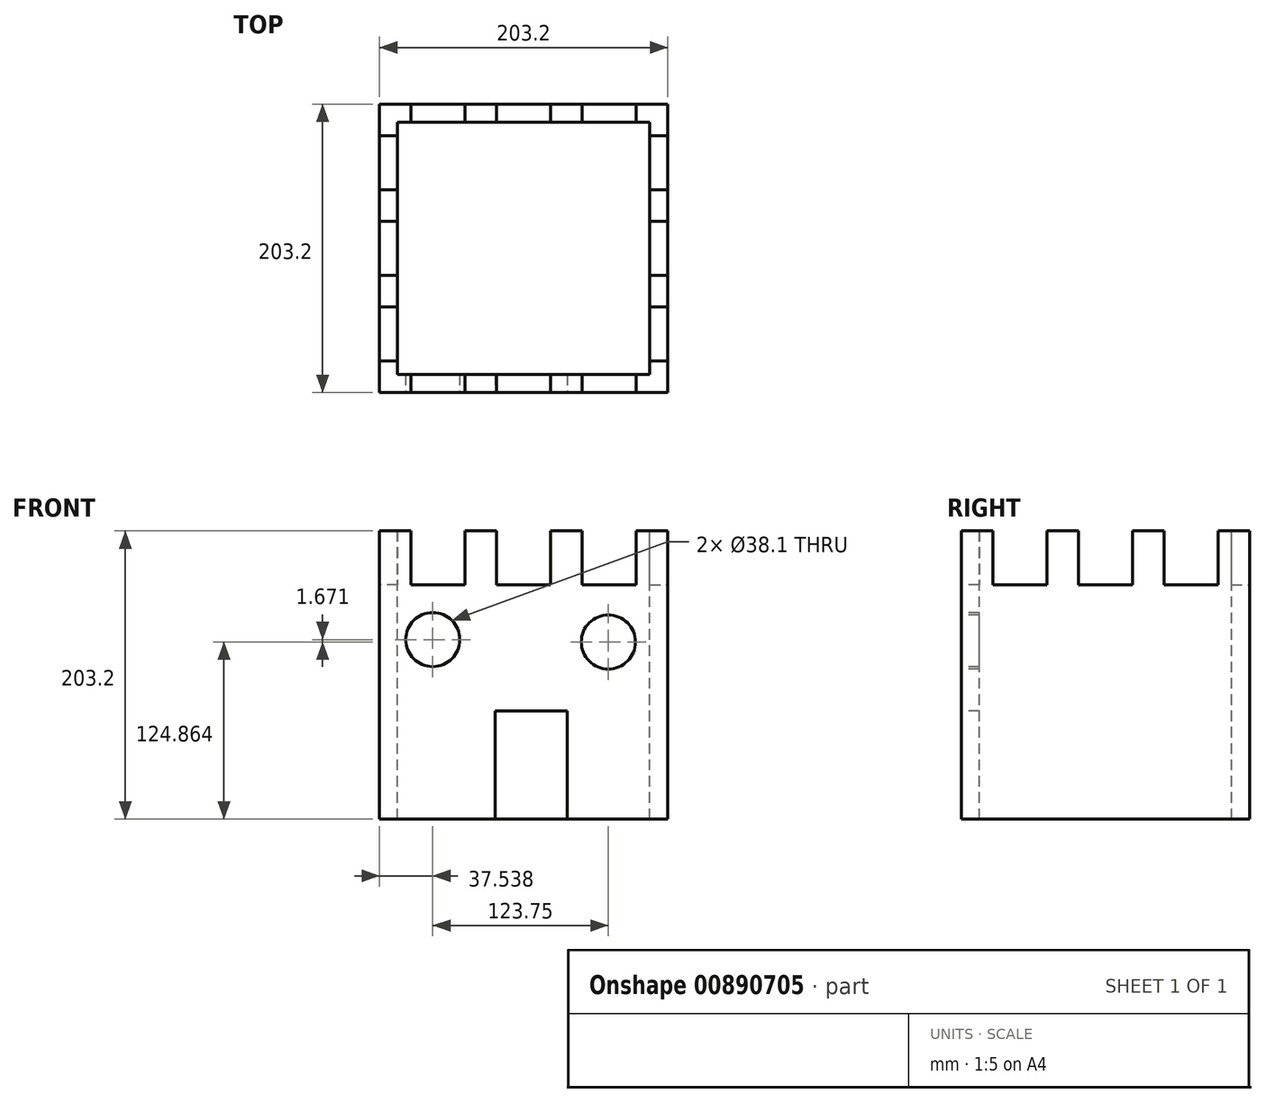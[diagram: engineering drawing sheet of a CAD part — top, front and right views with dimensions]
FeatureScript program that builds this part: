
annotation { "Feature Type Name" : "Feature", "Feature Type Description" : "" }
export const myFeature = defineFeature(function(context is Context, id is Id, definition is map)
    precondition{}
    {
        {
            var Q0;
            Q0=qCreatedBy(makeId("Front.planeOp"),FACE);
            var sketch = newSketch(context, id + "F0", { "sketchPlane" : qUnion([Q0])});
            skLineSegment(sketch, "E0.bottom", {"start": v(-101.6, 101.6) * mm, "end": v(101.6, 101.6) * mm});
            skLineSegment(sketch, "E0.top", {"start": v(-101.6, -101.6) * mm, "end": v(101.6, -101.6) * mm});
            skLineSegment(sketch, "E0.left", {"start": v(-101.6, 101.6) * mm, "end": v(-101.6, -101.6) * mm});
            skLineSegment(sketch, "E0.right", {"start": v(101.6, 101.6) * mm, "end": v(101.6, -101.6) * mm});
            skPoint(sketch, "E0.middle", {"position": v(0, 0) * mm});
            skSolve(sketch);
        }
        {
            var Q0;
            Q0=makeQuery(id+"F0.imprint","IMPRINT",FACE,{"disambiguationData":[TD([[makeQuery(id+"F0.imprint","IMPRINT",EDGE,{"derivedFrom":sQuery(id+"F0.wireOp",EDGE,"E0.bottom")}),-1.0]])]});
            extrude(context, id + "F1", {"entities" : qUnion([Q0]), "depth" : 203.2 * mm, "offsetDistance" : 25.4 * mm});
        }
        {
            var Q0;
            Q0=makeQuery(id+"F1.opExtrude","SWEPT_FACE",FACE,{"disambiguationData":[OSD([sQuery(id+"F0.wireOp",EDGE,"E0.bottom")])]});
            var sketch = newSketch(context, id + "F2", { "sketchPlane" : qUnion([Q0])});
            skLineSegment(sketch, "E1.bottom", {"start": v(-88.9, -12.7) * mm, "end": v(88.9, -12.7) * mm});
            skLineSegment(sketch, "E1.top", {"start": v(-88.9, -190.5) * mm, "end": v(88.9, -190.5) * mm});
            skLineSegment(sketch, "E1.left", {"start": v(-88.9, -12.7) * mm, "end": v(-88.9, -190.5) * mm});
            skLineSegment(sketch, "E1.right", {"start": v(88.9, -12.7) * mm, "end": v(88.9, -190.5) * mm});
            skPoint(sketch, "E1.middle", {"position": v(0, -101.6) * mm});
            skPoint(sketch, "E1.middle.positionSnap0", {"position": v(-101.6, -101.6) * mm});
            skPoint(sketch, "E1.centerSnap0", {"position": v(-101.6, -101.6) * mm});
            skSolve(sketch);
        }
        {
            var Q0;
            Q0=makeQuery(id+"F2.imprint","IMPRINT",FACE,{"disambiguationData":[TD([[makeQuery(id+"F2.imprint","IMPRINT",EDGE,{"derivedFrom":sQuery(id+"F2.wireOp",EDGE,"E1.bottom")}),-1.0]])]});
            extrude(context, id + "F3", {"entities" : qUnion([Q0]), "operationType" : NewBodyOperationType.REMOVE, "oppositeDirection" : true, "depth" : 203.2 * mm, "offsetDistance" : 25.4 * mm});
        }
        {
            var Q0;
            Q0=makeQuery(id+"F1.opExtrude","CAP_FACE",FACE,{"disambiguationData":[OSD([sQuery(id+"F0.wireOp",EDGE,"E0.bottom"),sQuery(id+"F0.wireOp",EDGE,"E0.top"),sQuery(id+"F0.wireOp",EDGE,"E0.left"),sQuery(id+"F0.wireOp",EDGE,"E0.right")])],"isStart":false});
            var sketch = newSketch(context, id + "F4", { "sketchPlane" : qUnion([Q0])});
            skLineSegment(sketch, "E2.bottom", {"start": v(-20.1, -101.6) * mm, "end": v(30.7, -101.6) * mm});
            skLineSegment(sketch, "E2.top", {"start": v(-20.1, -25.4) * mm, "end": v(30.7, -25.4) * mm});
            skLineSegment(sketch, "E2.left", {"start": v(-20.1, -101.6) * mm, "end": v(-20.1, -25.4) * mm});
            skLineSegment(sketch, "E2.right", {"start": v(30.7, -101.6) * mm, "end": v(30.7, -25.4) * mm});
            skSolve(sketch);
        }
        {
            var Q0;
            Q0=makeQuery(id+"F4.imprint","IMPRINT",FACE,{"disambiguationData":[TD([[makeQuery(id+"F4.imprint","IMPRINT",EDGE,{"derivedFrom":sQuery(id+"F4.wireOp",EDGE,"E2.bottom")}),1.0]])]});
            extrude(context, id + "F5", {"entities" : qUnion([Q0]), "operationType" : NewBodyOperationType.REMOVE, "oppositeDirection" : true, "depth" : 25.4 * mm, "offsetDistance" : 25.4 * mm});
        }
        {
            var Q0;
            Q0=makeQuery(id+"F1.opExtrude","CAP_FACE",FACE,{"disambiguationData":[OSD([sQuery(id+"F0.wireOp",EDGE,"E0.bottom"),sQuery(id+"F0.wireOp",EDGE,"E0.top"),sQuery(id+"F0.wireOp",EDGE,"E0.left"),sQuery(id+"F0.wireOp",EDGE,"E0.right")])],"isStart":false});
            var sketch = newSketch(context, id + "F6", { "sketchPlane" : qUnion([Q0])});
            skLineSegment(sketch, "E3.bottom", {"start": v(-79.37, 101.6) * mm, "end": v(-41.27, 101.6) * mm});
            skLineSegment(sketch, "E3.top", {"start": v(-79.37, 63.5) * mm, "end": v(-41.27, 63.5) * mm});
            skLineSegment(sketch, "E3.left", {"start": v(-79.37, 101.6) * mm, "end": v(-79.37, 63.5) * mm});
            skLineSegment(sketch, "E3.right", {"start": v(-41.27, 101.6) * mm, "end": v(-41.27, 63.5) * mm});
            skLineSegment(sketch, "E4.bottom", {"start": v(-19.05, 101.6) * mm, "end": v(19.05, 101.6) * mm});
            skLineSegment(sketch, "E4.top", {"start": v(-19.05, 63.5) * mm, "end": v(19.05, 63.5) * mm});
            skLineSegment(sketch, "E4.left", {"start": v(-19.05, 101.6) * mm, "end": v(-19.05, 63.5) * mm});
            skLineSegment(sketch, "E4.right", {"start": v(19.05, 101.6) * mm, "end": v(19.05, 63.5) * mm});
            skLineSegment(sketch, "E5.bottom", {"start": v(41.28, 101.6) * mm, "end": v(79.38, 101.6) * mm});
            skLineSegment(sketch, "E5.top", {"start": v(41.28, 63.5) * mm, "end": v(79.38, 63.5) * mm});
            skLineSegment(sketch, "E5.left", {"start": v(41.28, 101.6) * mm, "end": v(41.28, 63.5) * mm});
            skLineSegment(sketch, "E5.right", {"start": v(79.38, 101.6) * mm, "end": v(79.38, 63.5) * mm});
            skSolve(sketch);
        }
        {
            var Q0;
            Q0 = qSketchRegion(id + "F6", true);
            extrude(context, id + "F7", {"entities" : qUnion([Q0]), "operationType" : NewBodyOperationType.REMOVE, "oppositeDirection" : true, "depth" : 25.4 * mm, "offsetDistance" : 25.4 * mm});
        }
        {
            var Q0;
            Q0=makeQuery(id+"F1.opExtrude","SWEPT_FACE",FACE,{"disambiguationData":[OSD([sQuery(id+"F0.wireOp",EDGE,"E0.right")])]});
            var sketch = newSketch(context, id + "F8", { "sketchPlane" : qUnion([Q0])});
            skLineSegment(sketch, "E6.bottom", {"start": v(-180.98, 101.6) * mm, "end": v(-142.88, 101.6) * mm});
            skLineSegment(sketch, "E6.top", {"start": v(-180.98, 63.5) * mm, "end": v(-142.88, 63.5) * mm});
            skLineSegment(sketch, "E6.left", {"start": v(-180.98, 101.6) * mm, "end": v(-180.98, 63.5) * mm});
            skLineSegment(sketch, "E6.right", {"start": v(-142.88, 101.6) * mm, "end": v(-142.88, 63.5) * mm});
            skLineSegment(sketch, "E7.bottom", {"start": v(-120.65, 101.6) * mm, "end": v(-82.55, 101.6) * mm});
            skLineSegment(sketch, "E7.top", {"start": v(-120.65, 63.5) * mm, "end": v(-82.55, 63.5) * mm});
            skLineSegment(sketch, "E7.left", {"start": v(-120.65, 101.6) * mm, "end": v(-120.65, 63.5) * mm});
            skLineSegment(sketch, "E7.right", {"start": v(-82.55, 101.6) * mm, "end": v(-82.55, 63.5) * mm});
            skLineSegment(sketch, "E8.bottom", {"start": v(-60.33, 101.6) * mm, "end": v(-22.23, 101.6) * mm});
            skLineSegment(sketch, "E8.top", {"start": v(-60.33, 63.5) * mm, "end": v(-22.23, 63.5) * mm});
            skLineSegment(sketch, "E8.left", {"start": v(-60.33, 101.6) * mm, "end": v(-60.33, 63.5) * mm});
            skLineSegment(sketch, "E8.right", {"start": v(-22.23, 101.6) * mm, "end": v(-22.23, 63.5) * mm});
            skSolve(sketch);
        }
        {
            var Q0;
            Q0 = qSketchRegion(id + "F8", true);
            extrude(context, id + "F9", {"entities" : qUnion([Q0]), "operationType" : NewBodyOperationType.REMOVE, "oppositeDirection" : true, "depth" : 25.4 * mm, "offsetDistance" : 25.4 * mm});
        }
        {
            var Q0;
            Q0=makeQuery(id+"F1.opExtrude","CAP_FACE",FACE,{"disambiguationData":[OSD([sQuery(id+"F0.wireOp",EDGE,"E0.bottom"),sQuery(id+"F0.wireOp",EDGE,"E0.top"),sQuery(id+"F0.wireOp",EDGE,"E0.left"),sQuery(id+"F0.wireOp",EDGE,"E0.right")])],"isStart":true});
            var sketch = newSketch(context, id + "F10", { "sketchPlane" : qUnion([Q0])});
            skLineSegment(sketch, "E9.bottom", {"start": v(-79.38, 101.6) * mm, "end": v(-41.28, 101.6) * mm});
            skLineSegment(sketch, "E9.top", {"start": v(-79.38, 63.5) * mm, "end": v(-41.28, 63.5) * mm});
            skLineSegment(sketch, "E9.left", {"start": v(-79.38, 101.6) * mm, "end": v(-79.38, 63.5) * mm});
            skLineSegment(sketch, "E9.right", {"start": v(-41.28, 101.6) * mm, "end": v(-41.28, 63.5) * mm});
            skLineSegment(sketch, "E10.bottom", {"start": v(-19.05, 101.6) * mm, "end": v(19.05, 101.6) * mm});
            skLineSegment(sketch, "E10.top", {"start": v(-19.05, 63.5) * mm, "end": v(19.05, 63.5) * mm});
            skLineSegment(sketch, "E10.left", {"start": v(-19.05, 101.6) * mm, "end": v(-19.05, 63.5) * mm});
            skLineSegment(sketch, "E10.right", {"start": v(19.05, 101.6) * mm, "end": v(19.05, 63.5) * mm});
            skLineSegment(sketch, "E11.bottom", {"start": v(41.28, 101.6) * mm, "end": v(79.38, 101.6) * mm});
            skLineSegment(sketch, "E11.top", {"start": v(41.28, 63.5) * mm, "end": v(79.38, 63.5) * mm});
            skLineSegment(sketch, "E11.left", {"start": v(41.28, 101.6) * mm, "end": v(41.28, 63.5) * mm});
            skLineSegment(sketch, "E11.right", {"start": v(79.38, 101.6) * mm, "end": v(79.38, 63.5) * mm});
            skSolve(sketch);
        }
        {
            var Q0;
            Q0=makeQuery(id+"F10.imprint","IMPRINT",FACE,{"disambiguationData":[TD([[makeQuery(id+"F10.imprint","IMPRINT",EDGE,{"derivedFrom":sQuery(id+"F10.wireOp",EDGE,"E9.bottom")}),1.0]])]});
            var Q1;
            Q1=makeQuery(id+"F10.imprint","IMPRINT",FACE,{"disambiguationData":[TD([[makeQuery(id+"F10.imprint","IMPRINT",EDGE,{"derivedFrom":sQuery(id+"F10.wireOp",EDGE,"E10.bottom")}),1.0]])]});
            var Q2;
            Q2=makeQuery(id+"F10.imprint","IMPRINT",FACE,{"disambiguationData":[TD([[makeQuery(id+"F10.imprint","IMPRINT",EDGE,{"derivedFrom":sQuery(id+"F10.wireOp",EDGE,"E11.bottom")}),1.0]])]});
            extrude(context, id + "F11", {"entities" : qUnion([Q0, Q1, Q2]), "operationType" : NewBodyOperationType.REMOVE, "oppositeDirection" : true, "depth" : 25.4 * mm, "offsetDistance" : 25.4 * mm});
        }
        {
            var Q0;
            Q0=makeQuery(id+"F1.opExtrude","SWEPT_FACE",FACE,{"disambiguationData":[OSD([sQuery(id+"F0.wireOp",EDGE,"E0.left")])]});
            var sketch = newSketch(context, id + "F12", { "sketchPlane" : qUnion([Q0])});
            skLineSegment(sketch, "E12.bottom", {"start": v(22.23, 101.6) * mm, "end": v(60.33, 101.6) * mm});
            skLineSegment(sketch, "E12.top", {"start": v(22.23, 63.5) * mm, "end": v(60.33, 63.5) * mm});
            skLineSegment(sketch, "E12.left", {"start": v(22.23, 101.6) * mm, "end": v(22.23, 63.5) * mm});
            skLineSegment(sketch, "E12.right", {"start": v(60.33, 101.6) * mm, "end": v(60.33, 63.5) * mm});
            skLineSegment(sketch, "E13.bottom", {"start": v(82.55, 101.6) * mm, "end": v(120.65, 101.6) * mm});
            skLineSegment(sketch, "E13.top", {"start": v(82.55, 63.5) * mm, "end": v(120.65, 63.5) * mm});
            skLineSegment(sketch, "E13.left", {"start": v(82.55, 101.6) * mm, "end": v(82.55, 63.5) * mm});
            skLineSegment(sketch, "E13.right", {"start": v(120.65, 101.6) * mm, "end": v(120.65, 63.5) * mm});
            skLineSegment(sketch, "E14.bottom", {"start": v(142.88, 101.6) * mm, "end": v(180.97, 101.6) * mm});
            skLineSegment(sketch, "E14.top", {"start": v(142.88, 63.5) * mm, "end": v(180.97, 63.5) * mm});
            skLineSegment(sketch, "E14.left", {"start": v(142.88, 101.6) * mm, "end": v(142.88, 63.5) * mm});
            skLineSegment(sketch, "E14.right", {"start": v(180.97, 101.6) * mm, "end": v(180.97, 63.5) * mm});
            skSolve(sketch);
        }
        {
            var Q0;
            Q0 = qSketchRegion(id + "F12", true);
            extrude(context, id + "F13", {"entities" : qUnion([Q0]), "operationType" : NewBodyOperationType.REMOVE, "oppositeDirection" : true, "depth" : 25.4 * mm, "offsetDistance" : 25.4 * mm});
        }
        {
            var Q0;
            Q0=makeQuery(id+"F1.opExtrude","CAP_FACE",FACE,{"disambiguationData":[OSD([sQuery(id+"F0.wireOp",EDGE,"E0.bottom"),sQuery(id+"F0.wireOp",EDGE,"E0.top"),sQuery(id+"F0.wireOp",EDGE,"E0.left"),sQuery(id+"F0.wireOp",EDGE,"E0.right")])],"isStart":false});
            var sketch = newSketch(context, id + "F14", { "sketchPlane" : qUnion([Q0])});
            skCircle(sketch, "E15", {"center": v(-64.06, 24.94) * mm, "radius": 19.05 * mm});
            skCircle(sketch, "E16", {"center": v(59.69, 23.26) * mm, "radius": 19.05 * mm});
            skSolve(sketch);
        }
        {
            var Q0;
            Q0=makeQuery(id+"F14.imprint","IMPRINT",FACE,{"disambiguationData":[TD([[makeQuery(id+"F14.imprint","IMPRINT",EDGE,{"derivedFrom":sQuery(id+"F14.wireOp",EDGE,"E15")}),1.0]])]});
            var Q1;
            Q1=makeQuery(id+"F14.imprint","IMPRINT",FACE,{"disambiguationData":[TD([[makeQuery(id+"F14.imprint","IMPRINT",EDGE,{"derivedFrom":sQuery(id+"F14.wireOp",EDGE,"E16")}),1.0]])]});
            extrude(context, id + "F15", {"entities" : qUnion([Q0, Q1]), "operationType" : NewBodyOperationType.REMOVE, "oppositeDirection" : true, "depth" : 25.4 * mm, "offsetDistance" : 25.4 * mm});
        }
    });
